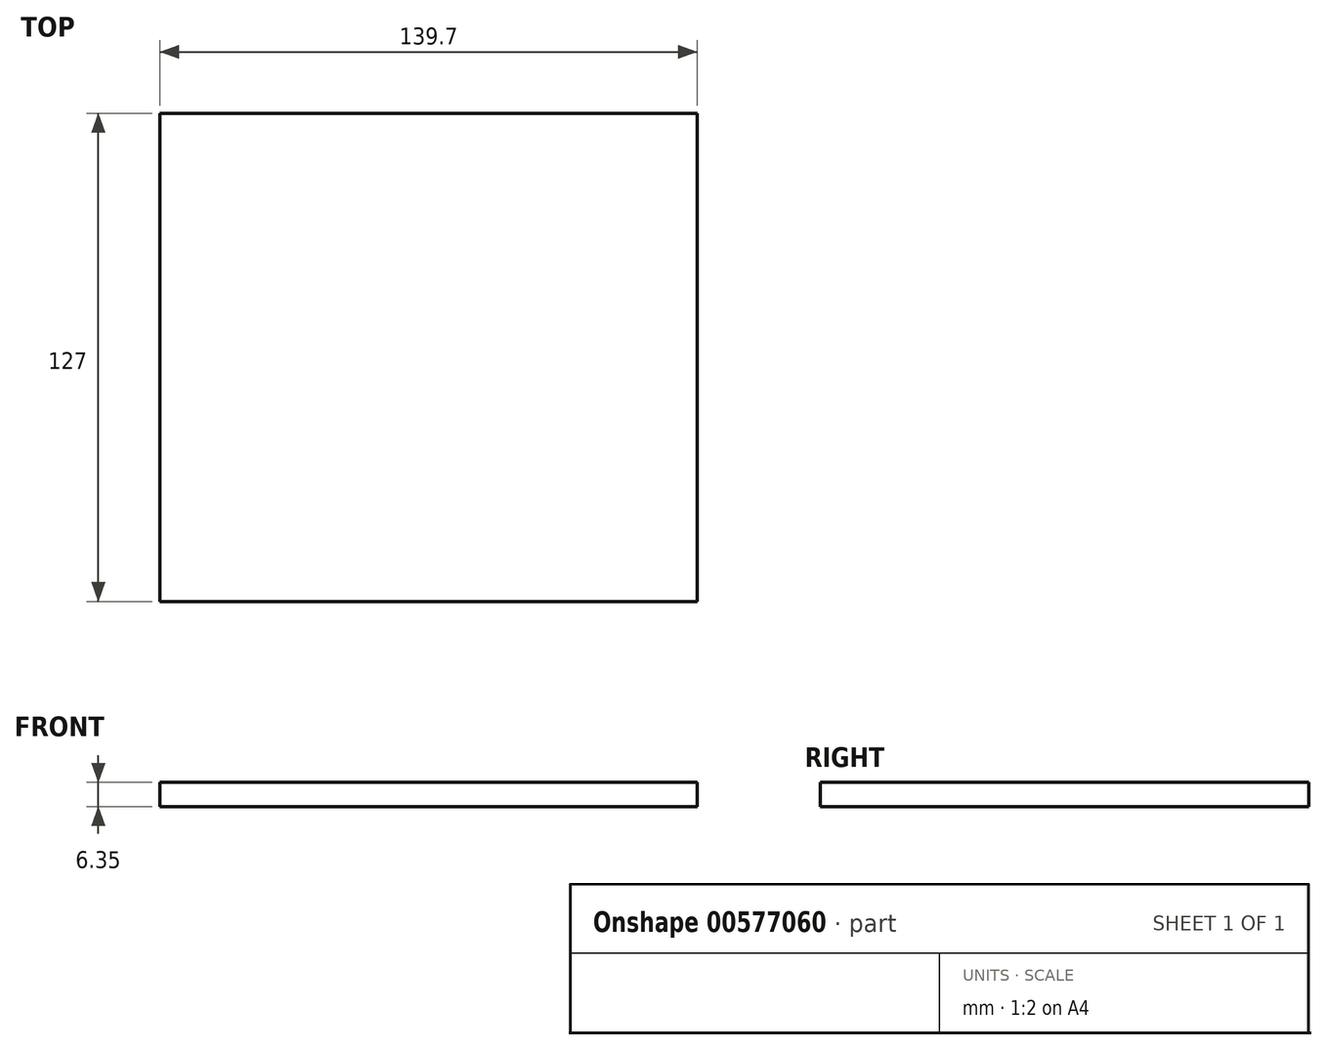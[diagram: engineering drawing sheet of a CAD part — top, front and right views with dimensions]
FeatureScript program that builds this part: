
annotation { "Feature Type Name" : "Feature", "Feature Type Description" : "" }
export const myFeature = defineFeature(function(context is Context, id is Id, definition is map)
    precondition{}
    {
        {
            var Q0;
            Q0=qCreatedBy(makeId("Top.planeOp"),FACE);
            var sketch = newSketch(context, id + "F0", { "sketchPlane" : qUnion([Q0])});
            skLineSegment(sketch, "E0.bottom", {"start": v(-76.74, 53.3) * mm, "end": v(62.96, 53.3) * mm});
            skLineSegment(sketch, "E0.top", {"start": v(-76.74, -73.7) * mm, "end": v(62.96, -73.7) * mm});
            skLineSegment(sketch, "E0.left", {"start": v(-76.74, 53.3) * mm, "end": v(-76.74, -73.7) * mm});
            skLineSegment(sketch, "E0.right", {"start": v(62.96, 53.3) * mm, "end": v(62.96, -73.7) * mm});
            skSolve(sketch);
        }
        {
            var Q0;
            Q0=makeQuery(id+"F0.imprint","IMPRINT",FACE,{"disambiguationData":[TD([[makeQuery(id+"F0.imprint","IMPRINT",EDGE,{"derivedFrom":sQuery(id+"F0.wireOp",EDGE,"E0.bottom")}),-1.0]])]});
            extrude(context, id + "F1", {"entities" : qUnion([Q0]), "depth" : 6.35 * mm, "offsetDistance" : 25.4 * mm});
        }
    });
